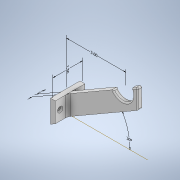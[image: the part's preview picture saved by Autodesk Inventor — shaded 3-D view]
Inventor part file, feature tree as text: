
AUTODESK INVENTOR PART (.ipt)
format: ipt  version: 2021.1 (Build 251245010, 245A)  size: 413,184 bytes
history: native  units: in
note: dims shown in document units (in); Inventor stores cm internally (conversion verified against a paired STEP export)
features: other x5, sketch x5, extrude x4, fillet x4, hole x1
ambient origin geometry x8: Origin, YZ Plane, XZ Plane, XY Plane, X Axis, Y Axis, Z Axis, Center Point
bodies: Solid2 (feature_tree)
feature tree (19):
  other  "Annotations"
  extrude  "Extrusion3"  Depth=0.25in
  extrude  "Extrusion4"  TaperAngle=30.0deg  [1 undecoded]
  sketch  "Sketch7"  dims[d26=1.075in d29=0.25in]
  extrude  "Extrusion5"  Depth=0.25in
  hole  "Hole3"  [1 undecoded]
  fillet  "Fillet3"  [1 undecoded]
  fillet  "Fillet4"  [1 undecoded]
  fillet  "Fillet5"  Radius=0.25in
  fillet  "Fillet6"  Radius=0.25in
  extrude  "Extrusion6"  Depth=0.0625in
  sketch  "Sketch5"  dims[d21=1.0in d22=0.25in]
  sketch  "Sketch6"  dims[d23=1.5in d24=0.0in d25=30.0deg]
  sketch  "Sketch8"  dims[d30=3.0in d31=0.25in d32=0.0in d33=0.0in d34=0.25in d35=0.25in]
  sketch  "Sketch9"  dims[d47=1.5in d48=0.0in d49=0.15in d50=0.75in d51=0.279in d52=0.25in d53=0.5635in d54=1.0in d55=0.8108in d65=0.0625in d66=0.0625in d67=0.0625in d68=0.125in d72=0.05in d73=0.0in d56=0.2085in d57=0.331in d58=1.5in d59=2.3174in d60=30.0deg d69=3.0in d70=0.3005in d71=0.25in]
  other  "Linear Dimension 1"
  other  "Angular Dimension 1"
  other  "Linear Dimension 2"
  other  "Linear Dimension 3"
note: 4 required parameter values undecoded (feature->parameter linkage not recoverable at this tier; creation-order binding heuristic only, values carry confidence <= 0.55)
